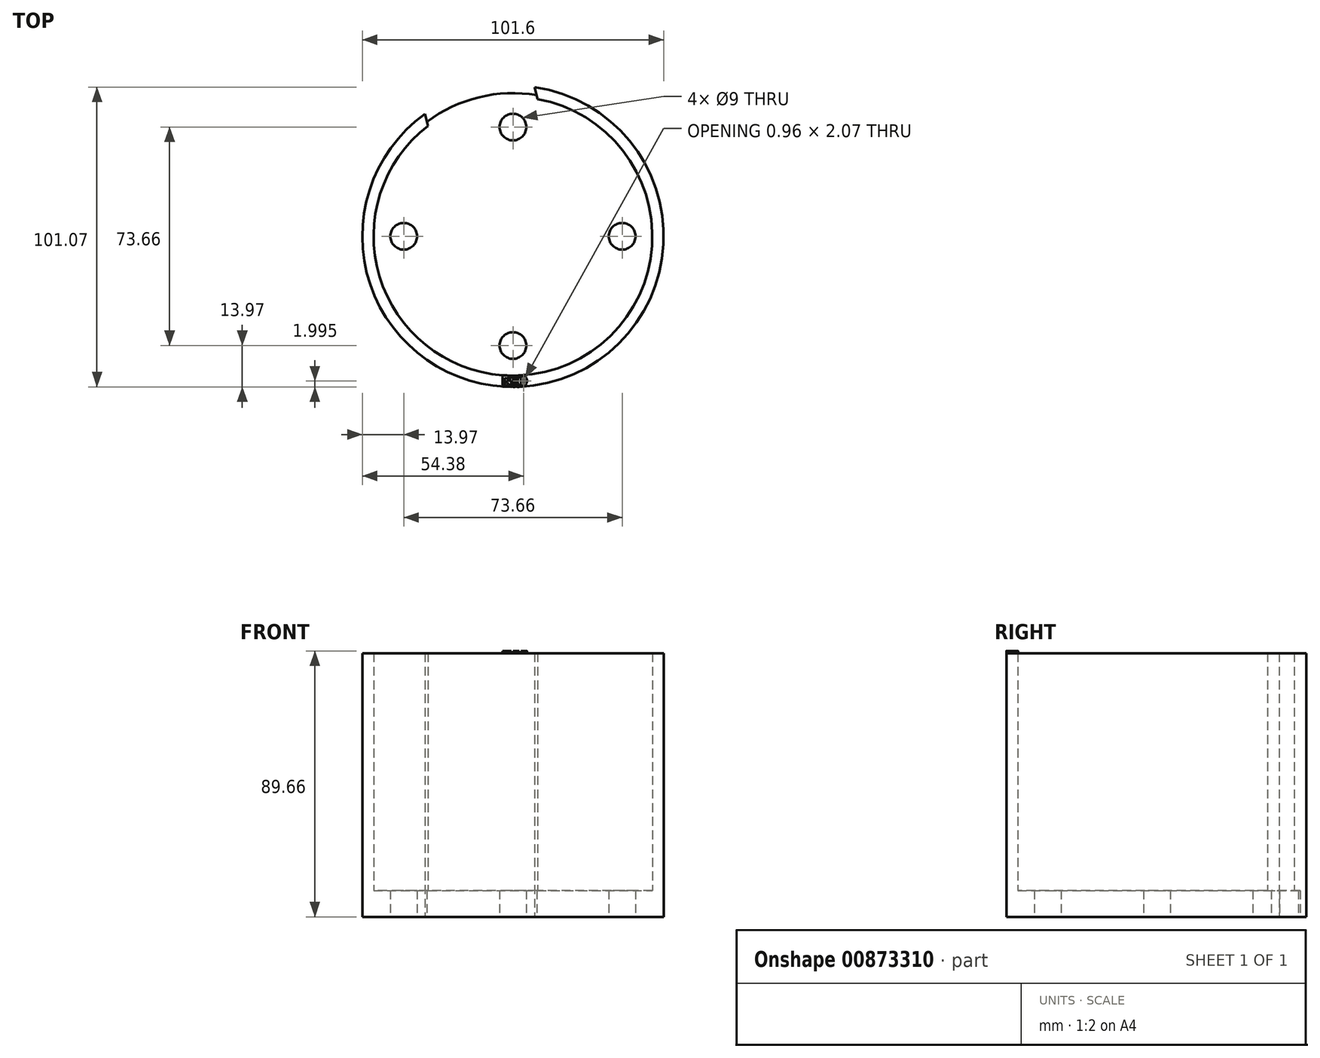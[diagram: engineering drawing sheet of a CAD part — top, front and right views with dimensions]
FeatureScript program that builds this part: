
annotation { "Feature Type Name" : "Feature", "Feature Type Description" : "" }
export const myFeature = defineFeature(function(context is Context, id is Id, definition is map)
    precondition{}
    {
        {
            var Q0;
            Q0=qCreatedBy(makeId("Top.planeOp"),FACE);
            var sketch = newSketch(context, id + "F0", { "sketchPlane" : qUnion([Q0])});
            skArc(sketch, "E0", {"start": v(-29.67, 41.24) * mm, "mid": v(12.04, -49.35) * mm, "end": v(7.35, 50.27) * mm});
            skArc(sketch, "E1", {"start": v(-28.69, 37.22) * mm, "mid": v(11.13, -45.65) * mm, "end": v(8.33, 46.25) * mm});
            skLineSegment(sketch, "E2", {"start": v(-28.69, 37.22) * mm, "end": v(-29.67, 41.24) * mm});
            skLineSegment(sketch, "E3", {"start": v(8.33, 46.25) * mm, "end": v(7.35, 50.27) * mm});
            skLineSegment(sketch, "E4", {"start": v(7.35, 50.27) * mm, "end": v(-29.67, 41.24) * mm});
            skLineSegment(sketch, "E5", {"start": v(-28.69, 37.22) * mm, "end": v(8.33, 46.25) * mm});
            skSolve(sketch);
        }
        {
            var Q0;
            Q0=makeQuery(id+"F0.imprint","IMPRINT",FACE,{"disambiguationData":[TD([[makeQuery(id+"F0.imprint","IMPRINT",EDGE,{"derivedFrom":sQuery(id+"F0.wireOp",EDGE,"E0")}),1.0]])]});
            extrude(context, id + "F1", {"entities" : qUnion([Q0]), "depth" : 88.9 * mm, "offsetDistance" : 25.4 * mm});
        }
        {
            var Q0;
            Q0=qCreatedBy(makeId("Top.planeOp"),FACE);
            var sketch = newSketch(context, id + "F2", { "sketchPlane" : qUnion([Q0])});
            skCircle(sketch, "E6", {"center": v(0, 0) * mm, "radius": 48.26 * mm});
            skSolve(sketch);
        }
        {
            var Q0;
            Q0=makeQuery(id+"F2.imprint","IMPRINT",FACE,{"disambiguationData":[TD([[makeQuery(id+"F2.imprint","IMPRINT",EDGE,{"derivedFrom":sQuery(id+"F2.wireOp",EDGE,"E6")}),1.0]])]});
            extrude(context, id + "F3", {"entities" : qUnion([Q0]), "operationType" : NewBodyOperationType.ADD, "depth" : 8.9 * mm, "offsetDistance" : 25.4 * mm});
        }
        {
            var Q0;
            Q0=qCreatedBy(makeId("Top.planeOp"),FACE);
            var sketch = newSketch(context, id + "F4", { "sketchPlane" : qUnion([Q0])});
            skCircle(sketch, "E7", {"center": v(0, 0) * mm, "radius": 40.64 * mm});
            skCircle(sketch, "E8", {"center": v(0, 0) * mm, "radius": 36.83 * mm});
            skCircle(sketch, "E9", {"center": v(0, 36.83) * mm, "radius": 3.81 * mm});
            skCircle(sketch, "E10", {"center": v(-36.83, 0) * mm, "radius": 3.81 * mm});
            skCircle(sketch, "E11", {"center": v(36.83, 0) * mm, "radius": 3.81 * mm});
            skCircle(sketch, "E12", {"center": v(0, -36.83) * mm, "radius": 3.81 * mm});
            skSolve(sketch);
        }
        {
            var Q0;
            Q0=sQuery(id+"F4.wireOp",VERTEX,"E12.center");
            var Q1;
            Q1=sQuery(id+"F4.wireOp",VERTEX,"E10.center");
            var Q2;
            Q2=sQuery(id+"F4.wireOp",VERTEX,"E9.center");
            var Q3;
            Q3=sQuery(id+"F4.wireOp",VERTEX,"E11.center");
            var Q4;
            Q4=makeQuery(id+"F1.opExtrude","SWEPT_BODY",BODY,{"disambiguationData":[OSD([sQuery(id+"F0.wireOp",EDGE,"E0"),sQuery(id+"F0.wireOp",EDGE,"E1"),sQuery(id+"F0.wireOp",EDGE,"E2"),sQuery(id+"F0.wireOp",EDGE,"E3")])]});
            hole(context, id + "F5", {"style" : HoleStyle.SIMPLE, "endStyle" : HoleEndStyle.THROUGH, "oppositeDirection" : true, "holeDiameter" : 9 * mm, "majorDiameter" : 6.35 * mm, "isTappedThrough" : true, "tappedDepth" : 12.7 * mm, "tapClearance" : 3, "locations" : qUnion([Q0, Q1, Q2, Q3]), "scope" : qUnion([Q4])});
        }
        {
            var Q0;
            Q0=makeQuery(id+"F1.opExtrude","CAP_FACE",FACE,{"disambiguationData":[OSD([sQuery(id+"F0.wireOp",EDGE,"E0"),sQuery(id+"F0.wireOp",EDGE,"E1"),sQuery(id+"F0.wireOp",EDGE,"E2"),sQuery(id+"F0.wireOp",EDGE,"E3")])],"isStart":false});
            var sketch = newSketch(context, id + "F6", { "sketchPlane" : qUnion([Q0])});
            skLineSegment(sketch, "E13", {"start": v(0, -47) * mm, "end": v(0, -50.8) * mm});
            skLineSegment(sketch, "E14", {"start": v(0, -47) * mm, "end": v(0.65, -46.99) * mm});
            skLineSegment(sketch, "E15", {"start": v(0.65, -46.99) * mm, "end": v(0.65, -50.8) * mm});
            skLineSegment(sketch, "E16", {"start": v(0.65, -50.8) * mm, "end": v(0, -50.8) * mm});
            skLineSegment(sketch, "E17", {"start": v(0.65, -48.9) * mm, "end": v(1.5, -46.97) * mm});
            skLineSegment(sketch, "E18", {"start": v(1.5, -46.97) * mm, "end": v(2.04, -46.95) * mm});
            skLineSegment(sketch, "E19", {"start": v(2.04, -46.95) * mm, "end": v(1.5, -48.9) * mm});
            skLineSegment(sketch, "E20", {"start": v(1.5, -48.9) * mm, "end": v(2.04, -50.76) * mm});
            skLineSegment(sketch, "E21", {"start": v(2.04, -50.76) * mm, "end": v(1.5, -50.9) * mm});
            skLineSegment(sketch, "E22", {"start": v(1.5, -50.9) * mm, "end": v(0.65, -48.9) * mm});
            skLineSegment(sketch, "E23", {"start": v(2.71, -46.91) * mm, "end": v(2.71, -50.73) * mm});
            skFitSpline(sketch, "E24", {"points": [v(2.71, -46.91) * mm, v(4.73, -48.68) * mm, v(2.71, -50.73) * mm], "startDerivative": vector(12.39, -2.55) * mm, "endDerivative": vector(-12.42, -3.6) * mm});
            skLineSegment(sketch, "E25", {"start": v(3.1, -47.77) * mm, "end": v(3.1, -49.84) * mm});
            skFitSpline(sketch, "E26", {"points": [v(3.1, -47.77) * mm, v(4.06, -48.68) * mm, v(3.1, -49.84) * mm], "startDerivative": vector(5.06, -0.9) * mm, "endDerivative": vector(-5.04, -0.28) * mm});
            skLineSegment(sketch, "E27", {"start": v(-0.55, -46.99) * mm, "end": v(-3.5, -46.86) * mm});
            skLineSegment(sketch, "E28", {"start": v(-3.5, -46.86) * mm, "end": v(-3.5, -50.68) * mm});
            skLineSegment(sketch, "E29", {"start": v(-3.5, -50.68) * mm, "end": v(-0.6, -50.8) * mm});
            skLineSegment(sketch, "E30", {"start": v(-0.6, -50.8) * mm, "end": v(-0.6, -48.68) * mm});
            skLineSegment(sketch, "E31", {"start": v(-0.6, -48.68) * mm, "end": v(-2.1, -48.68) * mm});
            skLineSegment(sketch, "E32", {"start": v(-2.1, -48.68) * mm, "end": v(-2.1, -49.74) * mm});
            skPoint(sketch, "E32.endSnap0", {"position": v(-0.6, -49.74) * mm});
            skLineSegment(sketch, "E33", {"start": v(-2.1, -49.74) * mm, "end": v(-1.36, -49.74) * mm});
            skLineSegment(sketch, "E34", {"start": v(-1.36, -49.74) * mm, "end": v(-1.36, -50.29) * mm});
            skLineSegment(sketch, "E35", {"start": v(-1.36, -50.29) * mm, "end": v(-2.72, -50.29) * mm});
            skLineSegment(sketch, "E36", {"start": v(-2.72, -50.29) * mm, "end": v(-2.72, -47.75) * mm});
            skLineSegment(sketch, "E37", {"start": v(-2.72, -47.75) * mm, "end": v(-0.55, -47.84) * mm});
            skLineSegment(sketch, "E38", {"start": v(-0.55, -47.84) * mm, "end": v(-0.55, -46.99) * mm});
            skSolve(sketch);
        }
        {
            var Q0;
            {var subQ6=sQuery(id+"F6.wireOp",EDGE,"E13");Q0=makeQuery(id+"F6.imprint","IMPRINT",FACE,{"disambiguationData":[TD([[makeQuery(id+"F6.imprint","IMPRINT",EDGE,{"derivedFrom":subQ6}),1.0]])]});}
            var Q1;
            {var subQ1=sQuery(id+"F6.wireOp",EDGE,"E17");Q1=makeQuery(id+"F6.imprint","IMPRINT",FACE,{"disambiguationData":[TD([[makeQuery(id+"F6.imprint","IMPRINT",EDGE,{"derivedFrom":subQ1}),-1.0]])]});}
            var Q2;
            Q2=makeQuery(id+"F6.imprint","IMPRINT",FACE,{"disambiguationData":[TD([[makeQuery(id+"F6.imprint","IMPRINT",EDGE,{"derivedFrom":sQuery(id+"F6.wireOp",EDGE,"E23")}),1.0]])]});
            var Q3;
            {var subQ3=sQuery(id+"F6.wireOp",EDGE,"E28");Q3=makeQuery(id+"F6.imprint","IMPRINT",FACE,{"disambiguationData":[TD([[makeQuery(id+"F6.imprint","IMPRINT",EDGE,{"derivedFrom":subQ3}),1.0]])]});}
            extrude(context, id + "F7", {"entities" : qUnion([Q0, Q1, Q2, Q3]), "depth" : 0.76 * mm, "offsetDistance" : 25.4 * mm});
        }
    });
